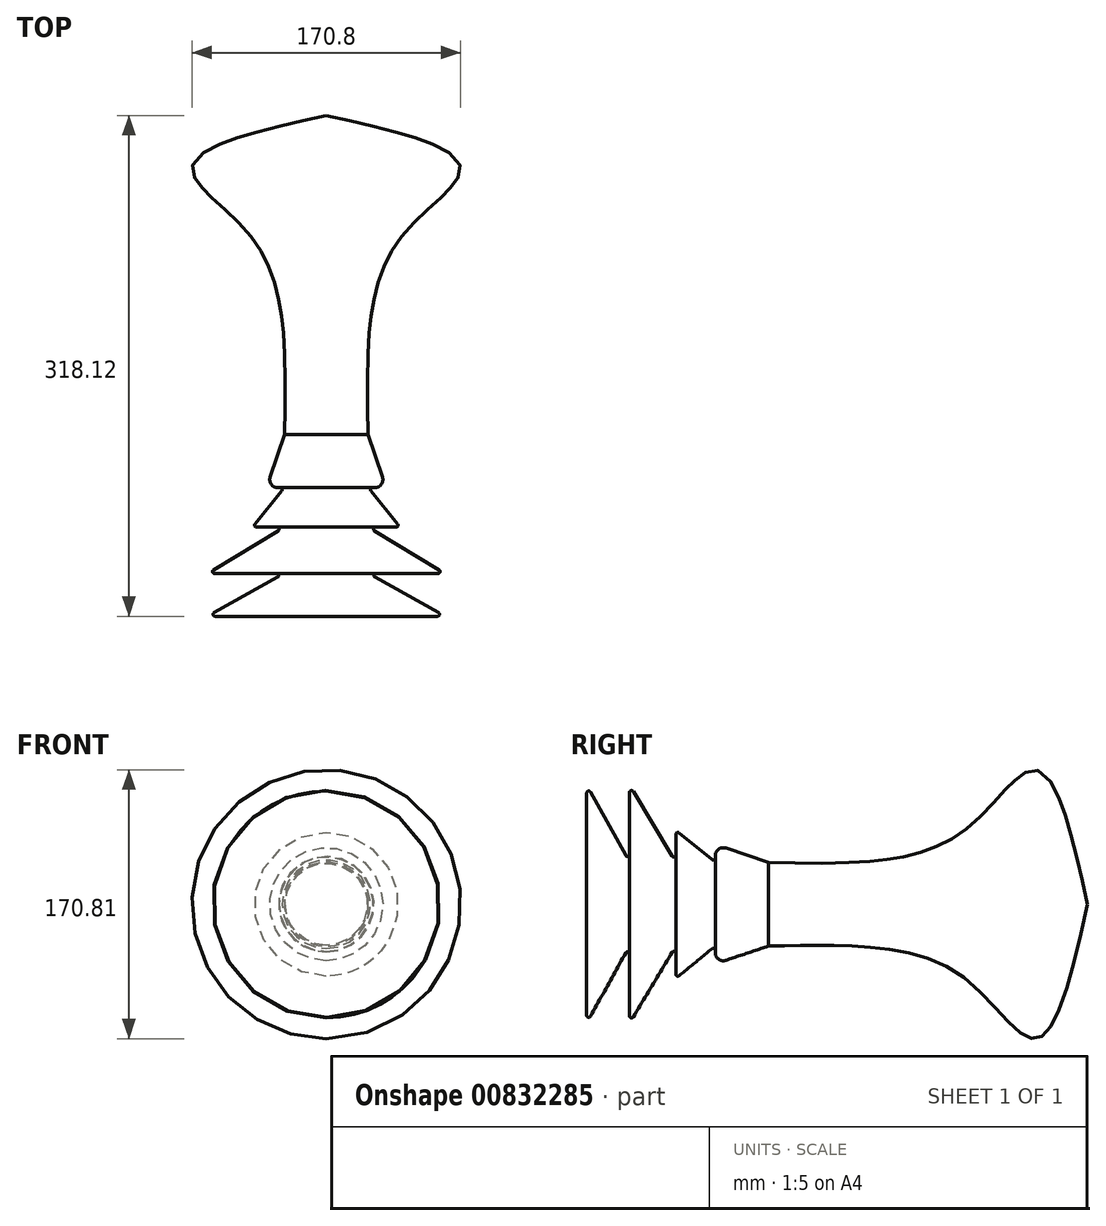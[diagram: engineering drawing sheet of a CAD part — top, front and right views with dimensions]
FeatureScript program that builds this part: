
annotation { "Feature Type Name" : "Feature", "Feature Type Description" : "" }
export const myFeature = defineFeature(function(context is Context, id is Id, definition is map)
    precondition{}
    {
        {
            var Q0;
            Q0=qCreatedBy(makeId("Right.planeOp"),FACE);
            var sketch = newSketch(context, id + "F0", { "sketchPlane" : qUnion([Q0])});
            skLineSegment(sketch, "E0", {"start": v(0, 0) * mm, "end": v(0, -48.92) * mm});
            skLineSegment(sketch, "E1", {"start": v(0, -48.92) * mm, "end": v(27.18, 0) * mm});
            skLineSegment(sketch, "E2", {"start": v(27.18, 0) * mm, "end": v(27.18, -48.92) * mm});
            skLineSegment(sketch, "E3", {"start": v(27.18, -48.92) * mm, "end": v(56.63, 0) * mm});
            skLineSegment(sketch, "E4", {"start": v(56.63, 0) * mm, "end": v(56.63, -20.5) * mm});
            skLineSegment(sketch, "E5", {"start": v(56.63, -20.5) * mm, "end": v(81.64, 0) * mm});
            skLineSegment(sketch, "E6", {"start": v(81.64, 0) * mm, "end": v(81.64, -11.29) * mm});
            skLineSegment(sketch, "E7", {"start": v(81.64, -11.29) * mm, "end": v(115.32, 0) * mm});
            skFitSpline(sketch, "E8", {"points": [v(115.32, 0) * mm, v(169.4, 0) * mm, v(239.8, -20.22) * mm, v(285.02, -58.76) * mm, v(318.12, 26.6) * mm], "startDerivative": vector(232.67, 6.36) * mm, "endDerivative": vector(97.78, 436.74) * mm});
            skLineSegment(sketch, "E9", {"start": v(0, 0) * mm, "end": v(0, 26.6) * mm});
            skLineSegment(sketch, "E10", {"start": v(0, 26.6) * mm, "end": v(318.12, 26.6) * mm});
            skSolve(sketch);
        }
        {
            var Q0;
            Q0=makeQuery(id+"F0.imprint","IMPRINT",FACE,{"disambiguationData":[TD([[makeQuery(id+"F0.imprint","IMPRINT",EDGE,{"derivedFrom":sQuery(id+"F0.wireOp",EDGE,"E0")}),1.0]])]});
            var Q1;
            Q1=sQuery(id+"F0.wireOp",EDGE,"E10");
            revolve(context, id + "F1", {"surfaceOperationType" : NewSurfaceOperationType.NEW, "entities" : qUnion([Q0]), "axis" : qUnion([Q1]), "revolveType" : RevolveType.FULL});
        }
        {
            var Q0;
            Q0=makeQuery(id+"F1.opRevolve","SWEPT_EDGE",EDGE,{"disambiguationData":[OSD([sQuery(id+"F0.wireOp",EDGE,"E6"),sQuery(id+"F0.wireOp",EDGE,"E7")])]});
            fillet(context, id + "F2", {"entities" : qUnion([Q0]), "radius" : 5.08 * mm, "tangentPropagation" : true, "allowEdgeOverflow" : false});
        }
        {
            var Q0;
            Q0=makeQuery(id+"F1.opRevolve","SWEPT_EDGE",EDGE,{"disambiguationData":[OSD([sQuery(id+"F0.wireOp",EDGE,"E5"),sQuery(id+"F0.wireOp",EDGE,"E6")])]});
            var Q1;
            Q1=makeQuery(id+"F1.opRevolve","SWEPT_EDGE",EDGE,{"disambiguationData":[OSD([sQuery(id+"F0.wireOp",EDGE,"E4"),sQuery(id+"F0.wireOp",EDGE,"E5")])]});
            var Q2;
            Q2=makeQuery(id+"F1.opRevolve","SWEPT_EDGE",EDGE,{"disambiguationData":[OSD([sQuery(id+"F0.wireOp",EDGE,"E3"),sQuery(id+"F0.wireOp",EDGE,"E4")])]});
            var Q3;
            Q3=makeQuery(id+"F1.opRevolve","SWEPT_EDGE",EDGE,{"disambiguationData":[OSD([sQuery(id+"F0.wireOp",EDGE,"E2"),sQuery(id+"F0.wireOp",EDGE,"E3")])]});
            var Q4;
            Q4=makeQuery(id+"F1.opRevolve","SWEPT_EDGE",EDGE,{"disambiguationData":[OSD([sQuery(id+"F0.wireOp",EDGE,"E1"),sQuery(id+"F0.wireOp",EDGE,"E2")])]});
            var Q5;
            Q5=makeQuery(id+"F1.opRevolve","SWEPT_EDGE",EDGE,{"disambiguationData":[OSD([sQuery(id+"F0.wireOp",EDGE,"E0"),sQuery(id+"F0.wireOp",EDGE,"E1")])]});
            fillet(context, id + "F3", {"entities" : qUnion([Q0, Q1, Q2, Q3, Q4, Q5]), "radius" : 1.27 * mm, "tangentPropagation" : true, "allowEdgeOverflow" : false});
        }
    });
